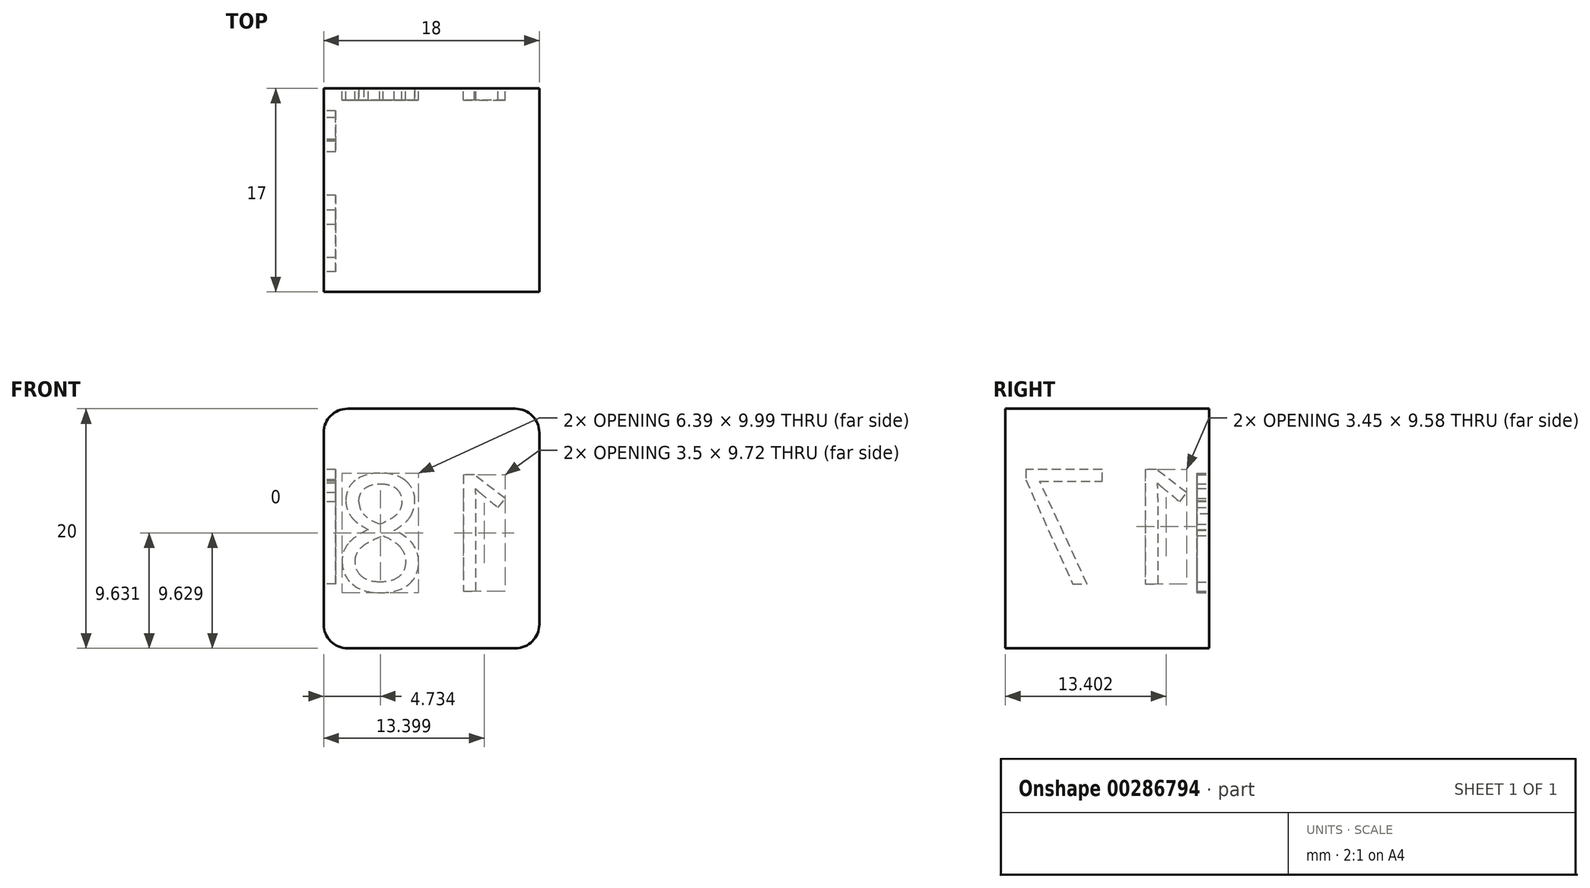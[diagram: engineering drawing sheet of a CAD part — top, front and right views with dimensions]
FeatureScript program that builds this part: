
annotation { "Feature Type Name" : "Feature", "Feature Type Description" : "" }
export const myFeature = defineFeature(function(context is Context, id is Id, definition is map)
    precondition{}
    {
        {
            var Q0;
            Q0=qCreatedBy(makeId("Top.planeOp"),FACE);
            var sketch = newSketch(context, id + "F0", { "sketchPlane" : qUnion([Q0])});
            skLineSegment(sketch, "E0.bottom", {"start": v(0, 0) * mm, "end": v(-18, 0) * mm});
            skLineSegment(sketch, "E0.top", {"start": v(0, 17) * mm, "end": v(-18, 17) * mm});
            skLineSegment(sketch, "E0.left", {"start": v(0, 0) * mm, "end": v(0, 17) * mm});
            skLineSegment(sketch, "E0.right", {"start": v(-18, 0) * mm, "end": v(-18, 17) * mm});
            skSolve(sketch);
        }
        {
            var Q0;
            Q0 = qSketchRegion(id + "F0", true);
            extrude(context, id + "F1", {"entities" : qUnion([Q0]), "depth" : 20 * mm});
        }
        {
            var Q0;
            Q0=makeQuery(id+"F1.opExtrude","SWEPT_FACE",FACE,{"disambiguationData":[OSD([sQuery(id+"F0.wireOp",EDGE,"E0.top")])]});
            var sketch = newSketch(context, id + "F2", { "sketchPlane" : qUnion([Q0])});
            skText(sketch, "E1", { "text": "18\n", "fontName": "OpenSans-Regular.ttf"});
            const initialGuessF2  = {"E1": [0.0016, 0.00477, 1, 0, 0.0098]};
            skSetInitialGuess(sketch, initialGuessF2);
            skSolve(sketch);
        }
        {
            var Q0;
            Q0 = qSketchRegion(id + "F2", true);
            extrude(context, id + "F3", {"entities" : qUnion([Q0]), "operationType" : NewBodyOperationType.REMOVE, "oppositeDirection" : true, "depth" : 1 * mm});
        }
        {
            var Q0;
            Q0=makeQuery(id+"F1.opExtrude","SWEPT_FACE",FACE,{"disambiguationData":[OSD([sQuery(id+"F0.wireOp",EDGE,"E0.right")])]});
            var sketch = newSketch(context, id + "F4", { "sketchPlane" : qUnion([Q0])});
            skText(sketch, "E2", { "text": "17", "fontName": "OpenSans-Regular.ttf"});
            const initialGuessF4  = {"E2": [-0.01636, 0.00536, 1, 0, 0.00966]};
            skSetInitialGuess(sketch, initialGuessF4);
            skSolve(sketch);
        }
        {
            var Q0;
            Q0 = qSketchRegion(id + "F4", true);
            extrude(context, id + "F5", {"entities" : qUnion([Q0]), "operationType" : NewBodyOperationType.REMOVE, "oppositeDirection" : true, "depth" : 1 * mm});
        }
        {
            var Q0;
            Q0=makeQuery(id+"F1.opExtrude","CAP_EDGE",EDGE,{"disambiguationData":[OSD([sQuery(id+"F0.wireOp",EDGE,"E0.left")])],"isStart":true});
            var Q1;
            Q1=makeQuery(id+"F1.opExtrude","CAP_EDGE",EDGE,{"disambiguationData":[OSD([sQuery(id+"F0.wireOp",EDGE,"E0.left")])],"isStart":false});
            var Q2;
            Q2=makeQuery(id+"F1.opExtrude","CAP_EDGE",EDGE,{"disambiguationData":[OSD([sQuery(id+"F0.wireOp",EDGE,"E0.right")])],"isStart":true});
            var Q3;
            Q3=makeQuery(id+"F1.opExtrude","CAP_EDGE",EDGE,{"disambiguationData":[OSD([sQuery(id+"F0.wireOp",EDGE,"E0.right")])],"isStart":false});
            fillet(context, id + "F6", {"entities" : qUnion([Q0, Q1, Q2, Q3]), "radius" : 2 * mm, "tangentPropagation" : true, "allowEdgeOverflow" : false});
        }
    });
